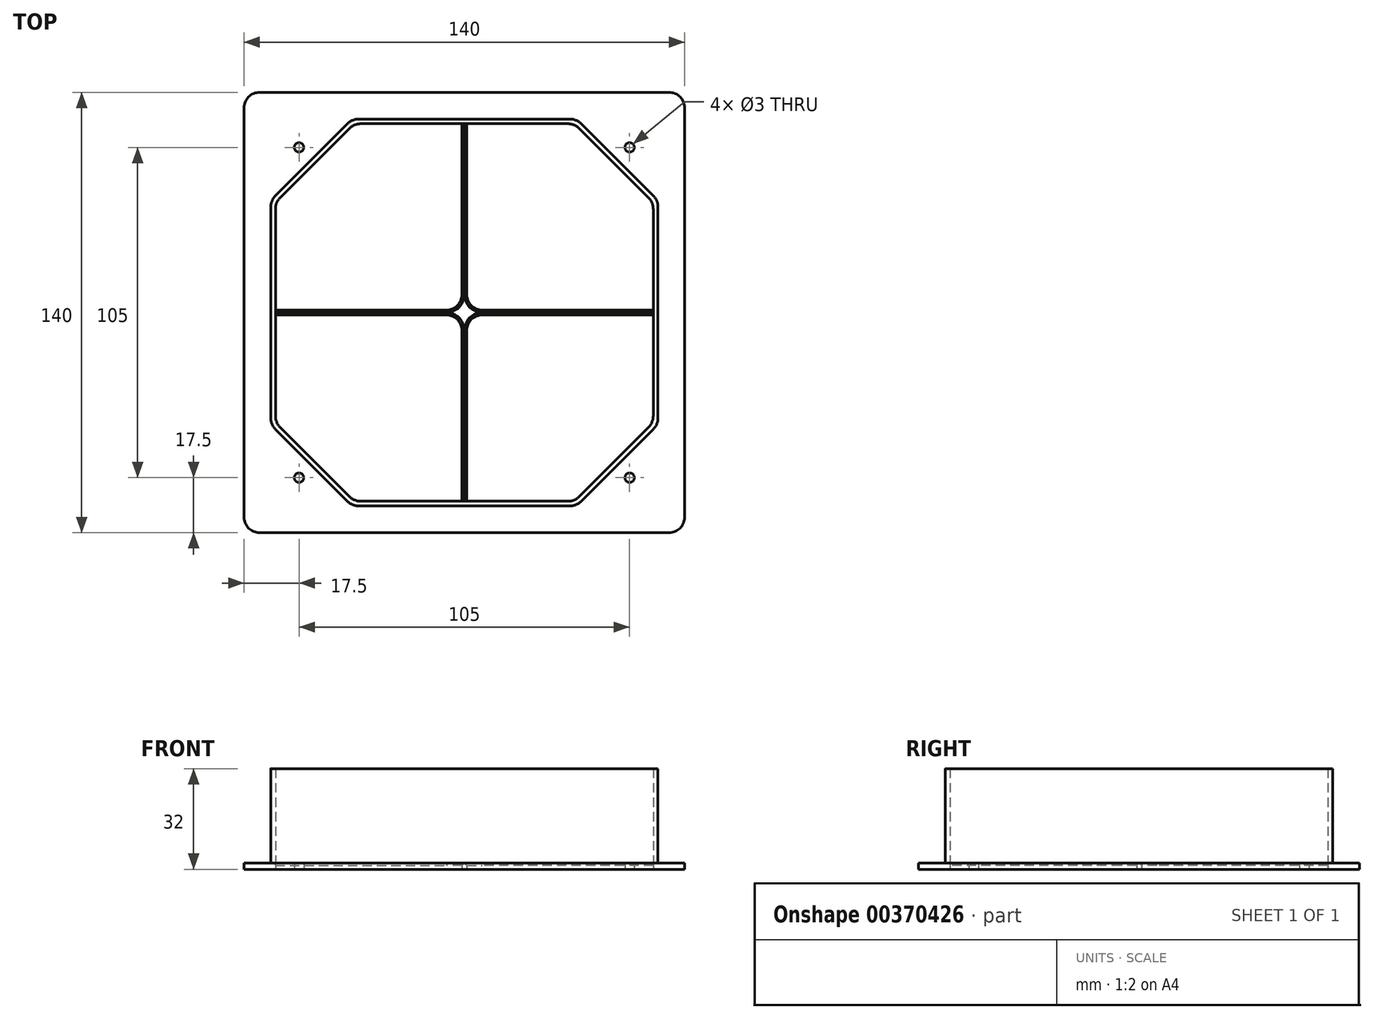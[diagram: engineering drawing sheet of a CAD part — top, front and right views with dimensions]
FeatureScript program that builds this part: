
annotation { "Feature Type Name" : "Feature", "Feature Type Description" : "" }
export const myFeature = defineFeature(function(context is Context, id is Id, definition is map)
    precondition{}
    {
        {
            var Q0;
            Q0=qCreatedBy(makeId("Top.planeOp"),FACE);
            var sketch = newSketch(context, id + "F0", { "sketchPlane" : qUnion([Q0])});
            skLineSegment(sketch, "E0", {"start": v(54, 35) * mm, "end": v(54, -35) * mm});
            skLineSegment(sketch, "E1", {"start": v(54, -35) * mm, "end": v(29, -60) * mm});
            skLineSegment(sketch, "E2", {"start": v(29, -60) * mm, "end": v(-41, -60) * mm});
            skLineSegment(sketch, "E3", {"start": v(-41, -60) * mm, "end": v(-66, -35) * mm});
            skLineSegment(sketch, "E4", {"start": v(-66, -35) * mm, "end": v(-66, 35) * mm});
            skLineSegment(sketch, "E5", {"start": v(-66, 35) * mm, "end": v(-41, 60) * mm});
            skLineSegment(sketch, "E6", {"start": v(-41, 60) * mm, "end": v(29, 60) * mm});
            skLineSegment(sketch, "E7", {"start": v(29, 60) * mm, "end": v(54, 35) * mm});
            skPoint(sketch, "E8.centerSnap0", {"position": v(54, 0) * mm});
            skLineSegment(sketch, "E9.bottom", {"start": v(64, -70) * mm, "end": v(-76, -70) * mm});
            skLineSegment(sketch, "E9.top", {"start": v(64, 70) * mm, "end": v(-76, 70) * mm});
            skLineSegment(sketch, "E9.left", {"start": v(64, -70) * mm, "end": v(64, 70) * mm});
            skLineSegment(sketch, "E9.right", {"start": v(-76, -70) * mm, "end": v(-76, 70) * mm});
            skPoint(sketch, "E9.middle", {"position": v(-6, 0) * mm});
            skPoint(sketch, "E9.middle.positionSnap0", {"position": v(-6, 60) * mm});
            skPoint(sketch, "E9.middle.positionSnap1", {"position": v(-66, 0) * mm});
            skPoint(sketch, "E9.centerSnap0", {"position": v(-6, 60) * mm});
            skPoint(sketch, "E9.centerSnap1", {"position": v(-66, 0) * mm});
            skPoint(sketch, "E10", {"position": v(-58.5, 52.5) * mm});
            skPoint(sketch, "E11", {"position": v(46.5, 52.5) * mm});
            skPoint(sketch, "E12", {"position": v(46.5, -52.5) * mm});
            skPoint(sketch, "E13", {"position": v(-58.5, -52.5) * mm});
            skLineSegment(sketch, "E14", {"start": v(-6.75, 60) * mm, "end": v(-6.75, -60) * mm});
            skLineSegment(sketch, "E15", {"start": v(-5.25, 60) * mm, "end": v(-5.25, -60) * mm});
            skLineSegment(sketch, "E16", {"start": v(-66, 0.75) * mm, "end": v(54, 0.75) * mm});
            skLineSegment(sketch, "E17", {"start": v(-66, -0.75) * mm, "end": v(54, -0.75) * mm});
            skLineSegment(sketch, "E18.0", {"start": v(29.62, -61.5) * mm, "end": v(-41.62, -61.5) * mm});
            skLineSegment(sketch, "E18.1", {"start": v(55.5, -35.62) * mm, "end": v(29.62, -61.5) * mm});
            skLineSegment(sketch, "E18.2", {"start": v(-41.62, -61.5) * mm, "end": v(-67.5, -35.62) * mm});
            skLineSegment(sketch, "E18.3", {"start": v(55.5, 35.62) * mm, "end": v(55.5, -35.62) * mm});
            skLineSegment(sketch, "E18.4", {"start": v(-67.5, -35.62) * mm, "end": v(-67.5, 35.62) * mm});
            skLineSegment(sketch, "E18.5", {"start": v(-67.5, 35.62) * mm, "end": v(-41.62, 61.5) * mm});
            skLineSegment(sketch, "E18.6", {"start": v(-41.62, 61.5) * mm, "end": v(29.62, 61.5) * mm});
            skLineSegment(sketch, "E18.7", {"start": v(29.62, 61.5) * mm, "end": v(55.5, 35.62) * mm});
            skSolve(sketch);
        }
        {
            var Q0;
            {var subQ0=sQuery(id+"F0.wireOp",EDGE,"E16");var subQ1=sQuery(id+"F0.wireOp",EDGE,"E4");var subQ2=makeQuery(id+"F0.imprint","INTERSECT",VERTEX,{"derivedFrom":[subQ1,subQ0]});Q0=makeQuery(id+"F0.imprint","IMPRINT",FACE,{"disambiguationData":[TD([[makeQuery(id+"F0.imprint","IMPRINT",EDGE,{"disambiguationData":[TD([[subQ2,1.0]])],"derivedFrom":subQ1}),-1.0]])]});}
            var Q1;
            {var subQ0=sQuery(id+"F0.wireOp",EDGE,"E14");var subQ1=sQuery(id+"F0.wireOp",EDGE,"E6");var subQ2=makeQuery(id+"F0.imprint","INTERSECT",VERTEX,{"derivedFrom":[subQ1,subQ0]});Q1=makeQuery(id+"F0.imprint","IMPRINT",FACE,{"disambiguationData":[TD([[makeQuery(id+"F0.imprint","IMPRINT",EDGE,{"disambiguationData":[TD([[subQ2,-1.0]])],"derivedFrom":subQ1}),-1.0]])]});}
            var Q2;
            {var subQ0=sQuery(id+"F0.wireOp",EDGE,"E14");var subQ1=sQuery(id+"F0.wireOp",EDGE,"E2");var subQ2=makeQuery(id+"F0.imprint","INTERSECT",VERTEX,{"derivedFrom":[subQ1,subQ0]});Q2=makeQuery(id+"F0.imprint","IMPRINT",FACE,{"disambiguationData":[TD([[makeQuery(id+"F0.imprint","IMPRINT",EDGE,{"disambiguationData":[TD([[subQ2,1.0]])],"derivedFrom":subQ1}),-1.0]])]});}
            var Q3;
            {var subQ0=sQuery(id+"F0.wireOp",EDGE,"E16");var subQ1=sQuery(id+"F0.wireOp",EDGE,"E0");var subQ2=makeQuery(id+"F0.imprint","INTERSECT",VERTEX,{"derivedFrom":[subQ1,subQ0]});Q3=makeQuery(id+"F0.imprint","IMPRINT",FACE,{"disambiguationData":[TD([[makeQuery(id+"F0.imprint","IMPRINT",EDGE,{"disambiguationData":[TD([[subQ2,-1.0]])],"derivedFrom":subQ1}),-1.0]])]});}
            var Q4;
            {var subQ0=sQuery(id+"F0.wireOp",EDGE,"E16");var subQ1=sQuery(id+"F0.wireOp",EDGE,"E14");var subQ2=makeQuery(id+"F0.imprint","INTERSECT",VERTEX,{"derivedFrom":[subQ1,subQ0]});Q4=makeQuery(id+"F0.imprint","IMPRINT",FACE,{"disambiguationData":[TD([[makeQuery(id+"F0.imprint","IMPRINT",EDGE,{"disambiguationData":[TD([[subQ2,-1.0]])],"derivedFrom":subQ1}),1.0]])]});}
            var Q5;
            Q5=makeQuery(id+"F0.imprint","IMPRINT",FACE,{"disambiguationData":[TD([[makeQuery(id+"F0.imprint","IMPRINT",EDGE,{"derivedFrom":sQuery(id+"F0.wireOp",EDGE,"E9.bottom")}),-1.0]])]});
            extrude(context, id + "F1", {"entities" : qUnion([Q0, Q1, Q2, Q3, Q4, Q5]), "depth" : 2 * mm});
        }
        {
            var Q0;
            {var subQ10=sQuery(id+"F0.wireOp",EDGE,"E1");Q0=makeQuery(id+"F0.imprint","IMPRINT",FACE,{"disambiguationData":[TD([[makeQuery(id+"F0.imprint","IMPRINT",EDGE,{"derivedFrom":subQ10}),1.0]])]});}
            extrude(context, id + "F2", {"entities" : qUnion([Q0]), "operationType" : NewBodyOperationType.ADD, "depth" : 32 * mm});
        }
        {
            var Q0;
            Q0=sQuery(id+"F0.wireOp",VERTEX,"E10");
            var Q1;
            Q1=sQuery(id+"F0.wireOp",VERTEX,"E13");
            var Q2;
            Q2=sQuery(id+"F0.wireOp",VERTEX,"E12");
            var Q3;
            Q3=sQuery(id+"F0.wireOp",VERTEX,"E11");
            var Q4;
            Q4=makeQuery(id+"F1.opExtrude","SWEPT_BODY",BODY,{"disambiguationData":[OSD([sQuery(id+"F0.wireOp",EDGE,"E0"),sQuery(id+"F0.wireOp",EDGE,"E1"),sQuery(id+"F0.wireOp",EDGE,"E2"),sQuery(id+"F0.wireOp",EDGE,"E3"),sQuery(id+"F0.wireOp",EDGE,"E4"),sQuery(id+"F0.wireOp",EDGE,"E5"),sQuery(id+"F0.wireOp",EDGE,"E6"),sQuery(id+"F0.wireOp",EDGE,"E7"),sQuery(id+"F0.wireOp",EDGE,"E9.bottom"),sQuery(id+"F0.wireOp",EDGE,"E9.top"),sQuery(id+"F0.wireOp",EDGE,"E9.left"),sQuery(id+"F0.wireOp",EDGE,"E9.right")])]});
            hole(context, id + "F3", {"style" : HoleStyle.SIMPLE, "endStyle" : HoleEndStyle.THROUGH, "oppositeDirection" : true, "holeDiameter" : 3 * mm, "isTappedThrough" : true, "tappedDepth" : 12 * mm, "tapClearance" : 3, "locations" : qUnion([Q0, Q1, Q2, Q3]), "scope" : qUnion([Q4])});
        }
        {
            var Q0;
            {var subQ0=sQuery(id+"F0.wireOp",EDGE,"E14");var subQ1=sQuery(id+"F0.wireOp",EDGE,"E6");Q0=makeQuery(id+"F2.boolean.opBoolean","SPLIT",EDGE,{"disambiguationData":[topologyDisambiguationEdgeConnected([makeQuery(id+"F2.opExtrude","SWEPT_FACE",FACE,{"disambiguationData":[OSD([subQ1])]})])],"derivedFrom":makeQuery(id+"F1.opExtrude","SWEPT_EDGE",EDGE,{"disambiguationData":[OSD([subQ1,subQ0])]})});}
            var Q1;
            Q1=makeQuery(id+"F1.opExtrude","SWEPT_EDGE",EDGE,{"disambiguationData":[OSD([sQuery(id+"F0.wireOp",EDGE,"E14"),sQuery(id+"F0.wireOp",EDGE,"E16")])]});
            var Q2;
            Q2=makeQuery(id+"F2.opExtrude","SWEPT_EDGE",EDGE,{"disambiguationData":[OSD([sQuery(id+"F0.wireOp",EDGE,"E5"),sQuery(id+"F0.wireOp",EDGE,"E6")])]});
            var Q3;
            Q3=makeQuery(id+"F2.opExtrude","SWEPT_EDGE",EDGE,{"disambiguationData":[OSD([sQuery(id+"F0.wireOp",EDGE,"E4"),sQuery(id+"F0.wireOp",EDGE,"E5")])]});
            var Q4;
            {var subQ0=sQuery(id+"F0.wireOp",EDGE,"E17");var subQ1=sQuery(id+"F0.wireOp",EDGE,"E4");Q4=makeQuery(id+"F2.boolean.opBoolean","SPLIT",EDGE,{"disambiguationData":[topologyDisambiguationEdgeConnected([makeQuery(id+"F2.opExtrude","SWEPT_FACE",FACE,{"disambiguationData":[OSD([subQ1])]})])],"derivedFrom":makeQuery(id+"F1.opExtrude","SWEPT_EDGE",EDGE,{"disambiguationData":[OSD([subQ1,subQ0])]})});}
            var Q5;
            {var subQ0=sQuery(id+"F0.wireOp",EDGE,"E16");var subQ1=sQuery(id+"F0.wireOp",EDGE,"E4");Q5=makeQuery(id+"F2.boolean.opBoolean","SPLIT",EDGE,{"disambiguationData":[topologyDisambiguationEdgeConnected([makeQuery(id+"F2.opExtrude","SWEPT_FACE",FACE,{"disambiguationData":[OSD([subQ1])]})])],"derivedFrom":makeQuery(id+"F1.opExtrude","SWEPT_EDGE",EDGE,{"disambiguationData":[OSD([subQ1,subQ0])]})});}
            var Q6;
            Q6=makeQuery(id+"F2.opExtrude","SWEPT_EDGE",EDGE,{"disambiguationData":[OSD([sQuery(id+"F0.wireOp",EDGE,"E3"),sQuery(id+"F0.wireOp",EDGE,"E4")])]});
            var Q7;
            Q7=makeQuery(id+"F1.opExtrude","SWEPT_EDGE",EDGE,{"disambiguationData":[OSD([sQuery(id+"F0.wireOp",EDGE,"E14"),sQuery(id+"F0.wireOp",EDGE,"E17")])]});
            var Q8;
            {var subQ0=sQuery(id+"F0.wireOp",EDGE,"E14");var subQ1=sQuery(id+"F0.wireOp",EDGE,"E2");Q8=makeQuery(id+"F2.boolean.opBoolean","SPLIT",EDGE,{"disambiguationData":[topologyDisambiguationEdgeConnected([makeQuery(id+"F2.opExtrude","SWEPT_FACE",FACE,{"disambiguationData":[OSD([subQ1])]})])],"derivedFrom":makeQuery(id+"F1.opExtrude","SWEPT_EDGE",EDGE,{"disambiguationData":[OSD([subQ1,subQ0])]})});}
            var Q9;
            Q9=makeQuery(id+"F2.opExtrude","SWEPT_EDGE",EDGE,{"disambiguationData":[OSD([sQuery(id+"F0.wireOp",EDGE,"E1"),sQuery(id+"F0.wireOp",EDGE,"E2")])]});
            var Q10;
            Q10=makeQuery(id+"F2.opExtrude","SWEPT_EDGE",EDGE,{"disambiguationData":[OSD([sQuery(id+"F0.wireOp",EDGE,"E0"),sQuery(id+"F0.wireOp",EDGE,"E1")])]});
            var Q11;
            {var subQ0=sQuery(id+"F0.wireOp",EDGE,"E17");var subQ1=sQuery(id+"F0.wireOp",EDGE,"E0");Q11=makeQuery(id+"F2.boolean.opBoolean","SPLIT",EDGE,{"disambiguationData":[topologyDisambiguationEdgeConnected([makeQuery(id+"F2.opExtrude","SWEPT_FACE",FACE,{"disambiguationData":[OSD([subQ1])]})])],"derivedFrom":makeQuery(id+"F1.opExtrude","SWEPT_EDGE",EDGE,{"disambiguationData":[OSD([subQ1,subQ0])]})});}
            var Q12;
            Q12=makeQuery(id+"F1.opExtrude","SWEPT_EDGE",EDGE,{"disambiguationData":[OSD([sQuery(id+"F0.wireOp",EDGE,"E15"),sQuery(id+"F0.wireOp",EDGE,"E17")])]});
            var Q13;
            {var subQ0=sQuery(id+"F0.wireOp",EDGE,"E15");var subQ1=sQuery(id+"F0.wireOp",EDGE,"E2");Q13=makeQuery(id+"F2.boolean.opBoolean","SPLIT",EDGE,{"disambiguationData":[topologyDisambiguationEdgeConnected([makeQuery(id+"F2.opExtrude","SWEPT_FACE",FACE,{"disambiguationData":[OSD([subQ1])]})])],"derivedFrom":makeQuery(id+"F1.opExtrude","SWEPT_EDGE",EDGE,{"disambiguationData":[OSD([subQ1,subQ0])]})});}
            var Q14;
            Q14=makeQuery(id+"F2.opExtrude","SWEPT_EDGE",EDGE,{"disambiguationData":[OSD([sQuery(id+"F0.wireOp",EDGE,"E6"),sQuery(id+"F0.wireOp",EDGE,"E7")])]});
            var Q15;
            Q15=makeQuery(id+"F2.opExtrude","SWEPT_EDGE",EDGE,{"disambiguationData":[OSD([sQuery(id+"F0.wireOp",EDGE,"E0"),sQuery(id+"F0.wireOp",EDGE,"E7")])]});
            var Q16;
            {var subQ0=sQuery(id+"F0.wireOp",EDGE,"E16");var subQ1=sQuery(id+"F0.wireOp",EDGE,"E0");Q16=makeQuery(id+"F2.boolean.opBoolean","SPLIT",EDGE,{"disambiguationData":[topologyDisambiguationEdgeConnected([makeQuery(id+"F2.opExtrude","SWEPT_FACE",FACE,{"disambiguationData":[OSD([subQ1])]})])],"derivedFrom":makeQuery(id+"F1.opExtrude","SWEPT_EDGE",EDGE,{"disambiguationData":[OSD([subQ1,subQ0])]})});}
            var Q17;
            Q17=makeQuery(id+"F1.opExtrude","SWEPT_EDGE",EDGE,{"disambiguationData":[OSD([sQuery(id+"F0.wireOp",EDGE,"E15"),sQuery(id+"F0.wireOp",EDGE,"E16")])]});
            var Q18;
            {var subQ0=sQuery(id+"F0.wireOp",EDGE,"E15");var subQ1=sQuery(id+"F0.wireOp",EDGE,"E6");Q18=makeQuery(id+"F2.boolean.opBoolean","SPLIT",EDGE,{"disambiguationData":[topologyDisambiguationEdgeConnected([makeQuery(id+"F2.opExtrude","SWEPT_FACE",FACE,{"disambiguationData":[OSD([subQ1])]})])],"derivedFrom":makeQuery(id+"F1.opExtrude","SWEPT_EDGE",EDGE,{"disambiguationData":[OSD([subQ1,subQ0])]})});}
            var Q19;
            Q19=makeQuery(id+"F2.opExtrude","SWEPT_EDGE",EDGE,{"disambiguationData":[OSD([sQuery(id+"F0.wireOp",EDGE,"E2"),sQuery(id+"F0.wireOp",EDGE,"E3")])]});
            var Q20;
            Q20=makeQuery(id+"F1.opExtrude","SWEPT_EDGE",EDGE,{"disambiguationData":[OSD([sQuery(id+"F0.wireOp",EDGE,"E9.bottom"),sQuery(id+"F0.wireOp",EDGE,"E9.right")])]});
            var Q21;
            Q21=makeQuery(id+"F1.opExtrude","SWEPT_EDGE",EDGE,{"disambiguationData":[OSD([sQuery(id+"F0.wireOp",EDGE,"E9.bottom"),sQuery(id+"F0.wireOp",EDGE,"E9.left")])]});
            var Q22;
            Q22=makeQuery(id+"F1.opExtrude","SWEPT_EDGE",EDGE,{"disambiguationData":[OSD([sQuery(id+"F0.wireOp",EDGE,"E9.top"),sQuery(id+"F0.wireOp",EDGE,"E9.left")])]});
            var Q23;
            Q23=makeQuery(id+"F1.opExtrude","SWEPT_EDGE",EDGE,{"disambiguationData":[OSD([sQuery(id+"F0.wireOp",EDGE,"E9.top"),sQuery(id+"F0.wireOp",EDGE,"E9.right")])]});
            var Q24;
            Q24=makeQuery(id+"F1.opExtrude","SWEPT_EDGE",EDGE,{"disambiguationData":[OSD([sQuery(id+"F0.wireOp",EDGE,"E18.5"),sQuery(id+"F0.wireOp",EDGE,"E18.6")])]});
            var Q25;
            Q25=makeQuery(id+"F1.opExtrude","SWEPT_EDGE",EDGE,{"disambiguationData":[OSD([sQuery(id+"F0.wireOp",EDGE,"E18.4"),sQuery(id+"F0.wireOp",EDGE,"E18.5")])]});
            var Q26;
            Q26=makeQuery(id+"F1.opExtrude","SWEPT_EDGE",EDGE,{"disambiguationData":[OSD([sQuery(id+"F0.wireOp",EDGE,"E18.6"),sQuery(id+"F0.wireOp",EDGE,"E18.7")])]});
            var Q27;
            Q27=makeQuery(id+"F1.opExtrude","SWEPT_EDGE",EDGE,{"disambiguationData":[OSD([sQuery(id+"F0.wireOp",EDGE,"E18.3"),sQuery(id+"F0.wireOp",EDGE,"E18.7")])]});
            var Q28;
            Q28=makeQuery(id+"F1.opExtrude","SWEPT_EDGE",EDGE,{"disambiguationData":[OSD([sQuery(id+"F0.wireOp",EDGE,"E18.1"),sQuery(id+"F0.wireOp",EDGE,"E18.3")])]});
            var Q29;
            Q29=makeQuery(id+"F1.opExtrude","SWEPT_EDGE",EDGE,{"disambiguationData":[OSD([sQuery(id+"F0.wireOp",EDGE,"E18.2"),sQuery(id+"F0.wireOp",EDGE,"E18.4")])]});
            var Q30;
            Q30=makeQuery(id+"F1.opExtrude","SWEPT_EDGE",EDGE,{"disambiguationData":[OSD([sQuery(id+"F0.wireOp",EDGE,"E18.0"),sQuery(id+"F0.wireOp",EDGE,"E18.2")])]});
            var Q31;
            Q31=makeQuery(id+"F2.opExtrude","SWEPT_EDGE",EDGE,{"disambiguationData":[OSD([sQuery(id+"F0.wireOp",EDGE,"E18.2"),sQuery(id+"F0.wireOp",EDGE,"E18.4")])]});
            var Q32;
            Q32=makeQuery(id+"F2.opExtrude","SWEPT_EDGE",EDGE,{"disambiguationData":[OSD([sQuery(id+"F0.wireOp",EDGE,"E18.0"),sQuery(id+"F0.wireOp",EDGE,"E18.2")])]});
            var Q33;
            Q33=makeQuery(id+"F2.opExtrude","SWEPT_EDGE",EDGE,{"disambiguationData":[OSD([sQuery(id+"F0.wireOp",EDGE,"E18.0"),sQuery(id+"F0.wireOp",EDGE,"E18.1")])]});
            var Q34;
            Q34=makeQuery(id+"F2.opExtrude","SWEPT_EDGE",EDGE,{"disambiguationData":[OSD([sQuery(id+"F0.wireOp",EDGE,"E18.1"),sQuery(id+"F0.wireOp",EDGE,"E18.3")])]});
            var Q35;
            Q35=makeQuery(id+"F2.opExtrude","SWEPT_EDGE",EDGE,{"disambiguationData":[OSD([sQuery(id+"F0.wireOp",EDGE,"E18.3"),sQuery(id+"F0.wireOp",EDGE,"E18.7")])]});
            var Q36;
            Q36=makeQuery(id+"F2.opExtrude","SWEPT_EDGE",EDGE,{"disambiguationData":[OSD([sQuery(id+"F0.wireOp",EDGE,"E18.6"),sQuery(id+"F0.wireOp",EDGE,"E18.7")])]});
            var Q37;
            Q37=makeQuery(id+"F2.opExtrude","SWEPT_EDGE",EDGE,{"disambiguationData":[OSD([sQuery(id+"F0.wireOp",EDGE,"E18.5"),sQuery(id+"F0.wireOp",EDGE,"E18.6")])]});
            var Q38;
            Q38=makeQuery(id+"F2.opExtrude","SWEPT_EDGE",EDGE,{"disambiguationData":[OSD([sQuery(id+"F0.wireOp",EDGE,"E18.4"),sQuery(id+"F0.wireOp",EDGE,"E18.5")])]});
            fillet(context, id + "F4", {"entities" : qUnion([Q0, Q1, Q2, Q3, Q4, Q5, Q6, Q7, Q8, Q9, Q10, Q11, Q12, Q13, Q14, Q15, Q16, Q17, Q18, Q19, Q20, Q21, Q22, Q23, Q24, Q25, Q26, Q27, Q28, Q29, Q30, Q31, Q32, Q33, Q34, Q35, Q36, Q37, Q38]), "radius" : 5 * mm, "tangentPropagation" : true, "allowEdgeOverflow" : false});
        }
        {
            var Q0;
            {var subQ0=sQuery(id+"F0.wireOp",EDGE,"E17");Q0=makeQuery(id+"F1.opExtrude","CAP_EDGE",EDGE,{"disambiguationData":[OSD([subQ0]),TDD([makeQuery(id+"F0.imprint","IMPRINT",EDGE,{"disambiguationData":[TD([[makeQuery(id+"F0.imprint","INTERSECT",VERTEX,{"derivedFrom":[sQuery(id+"F0.wireOp",EDGE,"E4"),subQ0]}),-1.0]])],"derivedFrom":subQ0})])],"isStart":false});}
            var Q1;
            {var subQ0=sQuery(id+"F0.wireOp",EDGE,"E17");Q1=makeQuery(id+"F1.opExtrude","CAP_EDGE",EDGE,{"disambiguationData":[OSD([subQ0]),TDD([makeQuery(id+"F0.imprint","IMPRINT",EDGE,{"disambiguationData":[TD([[makeQuery(id+"F0.imprint","INTERSECT",VERTEX,{"derivedFrom":[sQuery(id+"F0.wireOp",EDGE,"E0"),subQ0]}),1.0]])],"derivedFrom":subQ0})])],"isStart":false});}
            var Q2;
            {var subQ0=sQuery(id+"F0.wireOp",EDGE,"E15");Q2=makeQuery(id+"F1.opExtrude","CAP_EDGE",EDGE,{"disambiguationData":[OSD([subQ0]),TDD([makeQuery(id+"F0.imprint","IMPRINT",EDGE,{"disambiguationData":[TD([[makeQuery(id+"F0.imprint","INTERSECT",VERTEX,{"derivedFrom":[sQuery(id+"F0.wireOp",EDGE,"E6"),subQ0]}),-1.0]])],"derivedFrom":subQ0})])],"isStart":false});}
            var Q3;
            {var subQ0=sQuery(id+"F0.wireOp",EDGE,"E14");Q3=makeQuery(id+"F1.opExtrude","CAP_EDGE",EDGE,{"disambiguationData":[OSD([subQ0]),TDD([makeQuery(id+"F0.imprint","IMPRINT",EDGE,{"disambiguationData":[TD([[makeQuery(id+"F0.imprint","INTERSECT",VERTEX,{"derivedFrom":[sQuery(id+"F0.wireOp",EDGE,"E6"),subQ0]}),-1.0]])],"derivedFrom":subQ0})])],"isStart":false});}
            chamfer(context, id + "F5", {"entities" : qUnion([Q0, Q1, Q2, Q3]), "width" : 0.75 * mm, "tangentPropagation" : true});
        }
    });
